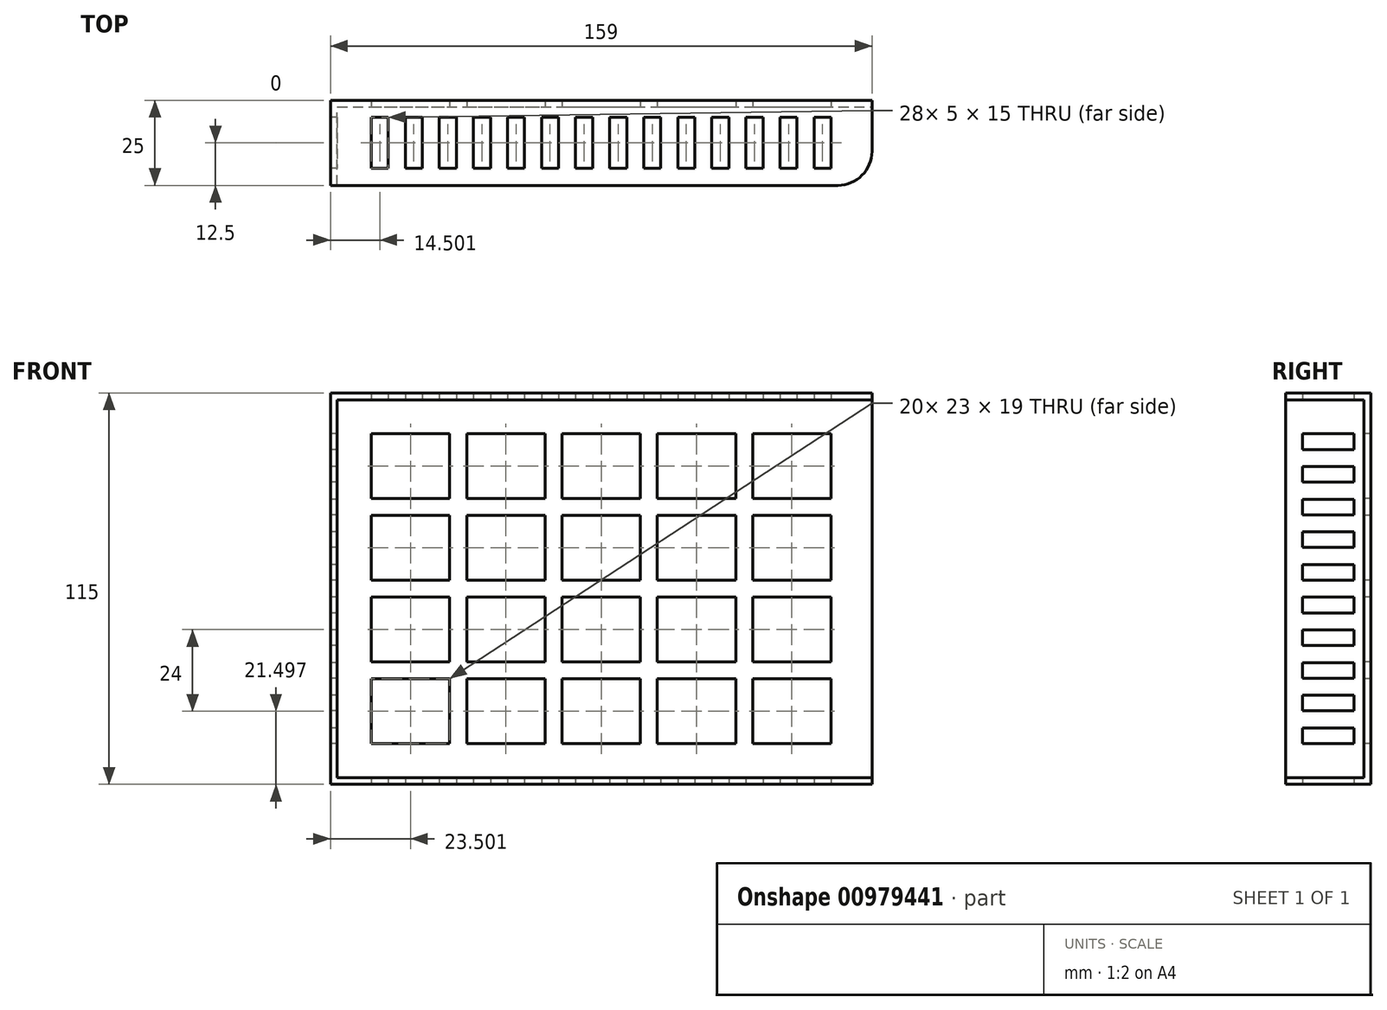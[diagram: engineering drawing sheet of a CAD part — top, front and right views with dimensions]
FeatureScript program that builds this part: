
annotation { "Feature Type Name" : "Feature", "Feature Type Description" : "" }
export const myFeature = defineFeature(function(context is Context, id is Id, definition is map)
    precondition{}
    {
        {
            var Q0;
            Q0=qCreatedBy(makeId("Front.planeOp"),FACE);
            var sketch = newSketch(context, id + "F0", { "sketchPlane" : qUnion([Q0])});
            skLineSegment(sketch, "E0.bottom", {"start": v(-112.02, 69.3) * mm, "end": v(46.98, 69.3) * mm});
            skLineSegment(sketch, "E0.top", {"start": v(-112.02, -45.7) * mm, "end": v(46.98, -45.7) * mm});
            skLineSegment(sketch, "E0.left", {"start": v(-112.02, 69.3) * mm, "end": v(-112.02, -45.7) * mm});
            skLineSegment(sketch, "E0.right", {"start": v(46.98, 69.3) * mm, "end": v(46.98, -45.7) * mm});
            skSolve(sketch);
        }
        {
            var Q0;
            Q0=makeQuery(id+"F0.imprint","IMPRINT",FACE,{"disambiguationData":[TD([[makeQuery(id+"F0.imprint","IMPRINT",EDGE,{"derivedFrom":sQuery(id+"F0.wireOp",EDGE,"E0.bottom")}),-1.0]])]});
            extrude(context, id + "F1", {"entities" : qUnion([Q0]), "depth" : 25 * mm, "offsetDistance" : 25 * mm});
        }
        {
            var Q0;
            Q0=makeQuery(id+"F1.opExtrude","CAP_FACE",FACE,{"disambiguationData":[OSD([sQuery(id+"F0.wireOp",EDGE,"E0.bottom"),sQuery(id+"F0.wireOp",EDGE,"E0.top"),sQuery(id+"F0.wireOp",EDGE,"E0.left"),sQuery(id+"F0.wireOp",EDGE,"E0.right")])],"isStart":false});
            var Q1;
            Q1=makeQuery(id+"F1.opExtrude","SWEPT_FACE",FACE,{"disambiguationData":[OSD([sQuery(id+"F0.wireOp",EDGE,"E0.right")])]});
            shell(context, id + "F2", {"entities" : qUnion([Q0, Q1]), "thickness" : 2 * mm});
        }
        {
            var Q0;
            Q0=makeQuery(id+"F1.opExtrude","CAP_EDGE",EDGE,{"disambiguationData":[OSD([sQuery(id+"F0.wireOp",EDGE,"E0.right")])],"isStart":false});
            var Q1;
            {var subQ0=sQuery(id+"F0.wireOp",EDGE,"E0.right");Q1=makeQuery(id+"F2.opShell","OFFSET_EDGE",EDGE,{"disambiguationData":[OSD([subQ0]),TDD([makeQuery(id+"F1.opExtrude","CAP_EDGE",EDGE,{"disambiguationData":[OSD([subQ0])],"isStart":false})])]});}
            fillet(context, id + "F3", {"entities" : qUnion([Q0, Q1]), "radius" : 10 * mm, "tangentPropagation" : true, "allowEdgeOverflow" : false});
        }
        {
            var Q0;
            Q0=makeQuery(id+"F2.opShell","OFFSET_FACE",FACE,{"disambiguationData":[OSD([sQuery(id+"F0.wireOp",EDGE,"E0.bottom"),sQuery(id+"F0.wireOp",EDGE,"E0.top"),sQuery(id+"F0.wireOp",EDGE,"E0.left"),sQuery(id+"F0.wireOp",EDGE,"E0.right")])]});
            var sketch = newSketch(context, id + "F4", { "sketchPlane" : qUnion([Q0])});
            skLineSegment(sketch, "E1.bottom", {"start": v(-100.02, 57.3) * mm, "end": v(-77.02, 57.3) * mm});
            skLineSegment(sketch, "E1.top", {"start": v(-100.02, 38.3) * mm, "end": v(-77.02, 38.3) * mm});
            skLineSegment(sketch, "E1.left", {"start": v(-100.02, 57.3) * mm, "end": v(-100.02, 38.3) * mm});
            skLineSegment(sketch, "E1.right", {"start": v(-77.02, 57.3) * mm, "end": v(-77.02, 38.3) * mm});
            skLineSegment(sketch, "E2.0.1.0", {"start": v(-100.02, 33.3) * mm, "end": v(-77.02, 33.3) * mm});
            skLineSegment(sketch, "E2.0.1.1", {"start": v(-77.02, 33.3) * mm, "end": v(-77.02, 14.3) * mm});
            skLineSegment(sketch, "E2.0.1.2", {"start": v(-100.02, 14.3) * mm, "end": v(-77.02, 14.3) * mm});
            skLineSegment(sketch, "E2.0.1.3", {"start": v(-100.02, 33.3) * mm, "end": v(-100.02, 14.3) * mm});
            skLineSegment(sketch, "E2.0.2.0", {"start": v(-100.02, 9.3) * mm, "end": v(-77.02, 9.3) * mm});
            skLineSegment(sketch, "E2.0.2.1", {"start": v(-77.02, 9.3) * mm, "end": v(-77.02, -9.7) * mm});
            skLineSegment(sketch, "E2.0.2.2", {"start": v(-100.02, -9.7) * mm, "end": v(-77.02, -9.7) * mm});
            skLineSegment(sketch, "E2.0.2.3", {"start": v(-100.02, 9.3) * mm, "end": v(-100.02, -9.7) * mm});
            skLineSegment(sketch, "E2.0.3.0", {"start": v(-100.02, -14.7) * mm, "end": v(-77.02, -14.7) * mm});
            skLineSegment(sketch, "E2.0.3.1", {"start": v(-77.02, -14.7) * mm, "end": v(-77.02, -33.7) * mm});
            skLineSegment(sketch, "E2.0.3.2", {"start": v(-100.02, -33.7) * mm, "end": v(-77.02, -33.7) * mm});
            skLineSegment(sketch, "E2.0.3.3", {"start": v(-100.02, -14.7) * mm, "end": v(-100.02, -33.7) * mm});
            skLineSegment(sketch, "E2.1.0.0", {"start": v(-72.02, 57.3) * mm, "end": v(-49.02, 57.3) * mm});
            skLineSegment(sketch, "E2.1.0.1", {"start": v(-49.02, 57.3) * mm, "end": v(-49.02, 38.3) * mm});
            skLineSegment(sketch, "E2.1.0.2", {"start": v(-72.02, 38.3) * mm, "end": v(-49.02, 38.3) * mm});
            skLineSegment(sketch, "E2.1.0.3", {"start": v(-72.02, 57.3) * mm, "end": v(-72.02, 38.3) * mm});
            skLineSegment(sketch, "E2.1.1.0", {"start": v(-72.02, 33.3) * mm, "end": v(-49.02, 33.3) * mm});
            skLineSegment(sketch, "E2.1.1.1", {"start": v(-49.02, 33.3) * mm, "end": v(-49.02, 14.3) * mm});
            skLineSegment(sketch, "E2.1.1.2", {"start": v(-72.02, 14.3) * mm, "end": v(-49.02, 14.3) * mm});
            skLineSegment(sketch, "E2.1.1.3", {"start": v(-72.02, 33.3) * mm, "end": v(-72.02, 14.3) * mm});
            skLineSegment(sketch, "E2.1.2.0", {"start": v(-72.02, 9.3) * mm, "end": v(-49.02, 9.3) * mm});
            skLineSegment(sketch, "E2.1.2.1", {"start": v(-49.02, 9.3) * mm, "end": v(-49.02, -9.7) * mm});
            skLineSegment(sketch, "E2.1.2.2", {"start": v(-72.02, -9.7) * mm, "end": v(-49.02, -9.7) * mm});
            skLineSegment(sketch, "E2.1.2.3", {"start": v(-72.02, 9.3) * mm, "end": v(-72.02, -9.7) * mm});
            skLineSegment(sketch, "E2.1.3.0", {"start": v(-72.02, -14.7) * mm, "end": v(-49.02, -14.7) * mm});
            skLineSegment(sketch, "E2.1.3.1", {"start": v(-49.02, -14.7) * mm, "end": v(-49.02, -33.7) * mm});
            skLineSegment(sketch, "E2.1.3.2", {"start": v(-72.02, -33.7) * mm, "end": v(-49.02, -33.7) * mm});
            skLineSegment(sketch, "E2.1.3.3", {"start": v(-72.02, -14.7) * mm, "end": v(-72.02, -33.7) * mm});
            skLineSegment(sketch, "E2.2.0.0", {"start": v(-44.02, 57.3) * mm, "end": v(-21.02, 57.3) * mm});
            skLineSegment(sketch, "E2.2.0.1", {"start": v(-21.02, 57.3) * mm, "end": v(-21.02, 38.3) * mm});
            skLineSegment(sketch, "E2.2.0.2", {"start": v(-44.02, 38.3) * mm, "end": v(-21.02, 38.3) * mm});
            skLineSegment(sketch, "E2.2.0.3", {"start": v(-44.02, 57.3) * mm, "end": v(-44.02, 38.3) * mm});
            skLineSegment(sketch, "E2.2.1.0", {"start": v(-44.02, 33.3) * mm, "end": v(-21.02, 33.3) * mm});
            skLineSegment(sketch, "E2.2.1.1", {"start": v(-21.02, 33.3) * mm, "end": v(-21.02, 14.3) * mm});
            skLineSegment(sketch, "E2.2.1.2", {"start": v(-44.02, 14.3) * mm, "end": v(-21.02, 14.3) * mm});
            skLineSegment(sketch, "E2.2.1.3", {"start": v(-44.02, 33.3) * mm, "end": v(-44.02, 14.3) * mm});
            skLineSegment(sketch, "E2.2.2.0", {"start": v(-44.02, 9.3) * mm, "end": v(-21.02, 9.3) * mm});
            skLineSegment(sketch, "E2.2.2.1", {"start": v(-21.02, 9.3) * mm, "end": v(-21.02, -9.7) * mm});
            skLineSegment(sketch, "E2.2.2.2", {"start": v(-44.02, -9.7) * mm, "end": v(-21.02, -9.7) * mm});
            skLineSegment(sketch, "E2.2.2.3", {"start": v(-44.02, 9.3) * mm, "end": v(-44.02, -9.7) * mm});
            skLineSegment(sketch, "E2.2.3.0", {"start": v(-44.02, -14.7) * mm, "end": v(-21.02, -14.7) * mm});
            skLineSegment(sketch, "E2.2.3.1", {"start": v(-21.02, -14.7) * mm, "end": v(-21.02, -33.7) * mm});
            skLineSegment(sketch, "E2.2.3.2", {"start": v(-44.02, -33.7) * mm, "end": v(-21.02, -33.7) * mm});
            skLineSegment(sketch, "E2.2.3.3", {"start": v(-44.02, -14.7) * mm, "end": v(-44.02, -33.7) * mm});
            skLineSegment(sketch, "E2.3.0.0", {"start": v(-16.02, 57.3) * mm, "end": v(6.98, 57.3) * mm});
            skLineSegment(sketch, "E2.3.0.1", {"start": v(6.98, 57.3) * mm, "end": v(6.98, 38.3) * mm});
            skLineSegment(sketch, "E2.3.0.2", {"start": v(-16.02, 38.3) * mm, "end": v(6.98, 38.3) * mm});
            skLineSegment(sketch, "E2.3.0.3", {"start": v(-16.02, 57.3) * mm, "end": v(-16.02, 38.3) * mm});
            skLineSegment(sketch, "E2.3.1.0", {"start": v(-16.02, 33.3) * mm, "end": v(6.98, 33.3) * mm});
            skLineSegment(sketch, "E2.3.1.1", {"start": v(6.98, 33.3) * mm, "end": v(6.98, 14.3) * mm});
            skLineSegment(sketch, "E2.3.1.2", {"start": v(-16.02, 14.3) * mm, "end": v(6.98, 14.3) * mm});
            skLineSegment(sketch, "E2.3.1.3", {"start": v(-16.02, 33.3) * mm, "end": v(-16.02, 14.3) * mm});
            skLineSegment(sketch, "E2.3.2.0", {"start": v(-16.02, 9.3) * mm, "end": v(6.98, 9.3) * mm});
            skLineSegment(sketch, "E2.3.2.1", {"start": v(6.98, 9.3) * mm, "end": v(6.98, -9.7) * mm});
            skLineSegment(sketch, "E2.3.2.2", {"start": v(-16.02, -9.7) * mm, "end": v(6.98, -9.7) * mm});
            skLineSegment(sketch, "E2.3.2.3", {"start": v(-16.02, 9.3) * mm, "end": v(-16.02, -9.7) * mm});
            skLineSegment(sketch, "E2.3.3.0", {"start": v(-16.02, -14.7) * mm, "end": v(6.98, -14.7) * mm});
            skLineSegment(sketch, "E2.3.3.1", {"start": v(6.98, -14.7) * mm, "end": v(6.98, -33.7) * mm});
            skLineSegment(sketch, "E2.3.3.2", {"start": v(-16.02, -33.7) * mm, "end": v(6.98, -33.7) * mm});
            skLineSegment(sketch, "E2.3.3.3", {"start": v(-16.02, -14.7) * mm, "end": v(-16.02, -33.7) * mm});
            skLineSegment(sketch, "E2.4.0.0", {"start": v(11.98, 57.3) * mm, "end": v(34.98, 57.3) * mm});
            skLineSegment(sketch, "E2.4.0.1", {"start": v(34.98, 57.3) * mm, "end": v(34.98, 38.3) * mm});
            skLineSegment(sketch, "E2.4.0.2", {"start": v(11.98, 38.3) * mm, "end": v(34.98, 38.3) * mm});
            skLineSegment(sketch, "E2.4.0.3", {"start": v(11.98, 57.3) * mm, "end": v(11.98, 38.3) * mm});
            skLineSegment(sketch, "E2.4.1.0", {"start": v(11.98, 33.3) * mm, "end": v(34.98, 33.3) * mm});
            skLineSegment(sketch, "E2.4.1.1", {"start": v(34.98, 33.3) * mm, "end": v(34.98, 14.3) * mm});
            skLineSegment(sketch, "E2.4.1.2", {"start": v(11.98, 14.3) * mm, "end": v(34.98, 14.3) * mm});
            skLineSegment(sketch, "E2.4.1.3", {"start": v(11.98, 33.3) * mm, "end": v(11.98, 14.3) * mm});
            skLineSegment(sketch, "E2.4.2.0", {"start": v(11.98, 9.3) * mm, "end": v(34.98, 9.3) * mm});
            skLineSegment(sketch, "E2.4.2.1", {"start": v(34.98, 9.3) * mm, "end": v(34.98, -9.7) * mm});
            skLineSegment(sketch, "E2.4.2.2", {"start": v(11.98, -9.7) * mm, "end": v(34.98, -9.7) * mm});
            skLineSegment(sketch, "E2.4.2.3", {"start": v(11.98, 9.3) * mm, "end": v(11.98, -9.7) * mm});
            skLineSegment(sketch, "E2.4.3.0", {"start": v(11.98, -14.7) * mm, "end": v(34.98, -14.7) * mm});
            skLineSegment(sketch, "E2.4.3.1", {"start": v(34.98, -14.7) * mm, "end": v(34.98, -33.7) * mm});
            skLineSegment(sketch, "E2.4.3.2", {"start": v(11.98, -33.7) * mm, "end": v(34.98, -33.7) * mm});
            skLineSegment(sketch, "E2.4.3.3", {"start": v(11.98, -14.7) * mm, "end": v(11.98, -33.7) * mm});
            skLineSegment(sketch, "E2.direction1", {"start": v(-100.02, 57.3) * mm, "end": v(-72.02, 57.3) * mm, "construction": true});
            skLineSegment(sketch, "E2.direction2", {"start": v(-100.02, 57.3) * mm, "end": v(-100.02, 33.3) * mm, "construction": true});
            skPoint(sketch, "E3.top.end.orphan", {"position": v(-100.02, -33.7) * mm});
            skSolve(sketch);
        }
        {
            var Q0;
            Q0=makeQuery(id+"F4.imprint","IMPRINT",FACE,{"disambiguationData":[TD([[makeQuery(id+"F4.imprint","IMPRINT",EDGE,{"derivedFrom":sQuery(id+"F4.wireOp",EDGE,"E1.bottom")}),-1.0]])]});
            var Q1;
            Q1=makeQuery(id+"F4.imprint","IMPRINT",FACE,{"disambiguationData":[TD([[makeQuery(id+"F4.imprint","IMPRINT",EDGE,{"derivedFrom":sQuery(id+"F4.wireOp",EDGE,"E2.1.0.0")}),-1.0]])]});
            var Q2;
            Q2=makeQuery(id+"F4.imprint","IMPRINT",FACE,{"disambiguationData":[TD([[makeQuery(id+"F4.imprint","IMPRINT",EDGE,{"derivedFrom":sQuery(id+"F4.wireOp",EDGE,"E2.2.0.0")}),-1.0]])]});
            var Q3;
            Q3=makeQuery(id+"F4.imprint","IMPRINT",FACE,{"disambiguationData":[TD([[makeQuery(id+"F4.imprint","IMPRINT",EDGE,{"derivedFrom":sQuery(id+"F4.wireOp",EDGE,"E2.3.0.0")}),-1.0]])]});
            var Q4;
            Q4=makeQuery(id+"F4.imprint","IMPRINT",FACE,{"disambiguationData":[TD([[makeQuery(id+"F4.imprint","IMPRINT",EDGE,{"derivedFrom":sQuery(id+"F4.wireOp",EDGE,"E2.4.0.0")}),-1.0]])]});
            var Q5;
            Q5=makeQuery(id+"F4.imprint","IMPRINT",FACE,{"disambiguationData":[TD([[makeQuery(id+"F4.imprint","IMPRINT",EDGE,{"derivedFrom":sQuery(id+"F4.wireOp",EDGE,"E2.0.1.0")}),-1.0]])]});
            var Q6;
            Q6=makeQuery(id+"F4.imprint","IMPRINT",FACE,{"disambiguationData":[TD([[makeQuery(id+"F4.imprint","IMPRINT",EDGE,{"derivedFrom":sQuery(id+"F4.wireOp",EDGE,"E2.1.1.0")}),-1.0]])]});
            var Q7;
            Q7=makeQuery(id+"F4.imprint","IMPRINT",FACE,{"disambiguationData":[TD([[makeQuery(id+"F4.imprint","IMPRINT",EDGE,{"derivedFrom":sQuery(id+"F4.wireOp",EDGE,"E2.2.1.0")}),-1.0]])]});
            var Q8;
            Q8=makeQuery(id+"F4.imprint","IMPRINT",FACE,{"disambiguationData":[TD([[makeQuery(id+"F4.imprint","IMPRINT",EDGE,{"derivedFrom":sQuery(id+"F4.wireOp",EDGE,"E2.3.1.0")}),-1.0]])]});
            var Q9;
            Q9=makeQuery(id+"F4.imprint","IMPRINT",FACE,{"disambiguationData":[TD([[makeQuery(id+"F4.imprint","IMPRINT",EDGE,{"derivedFrom":sQuery(id+"F4.wireOp",EDGE,"E2.4.1.0")}),-1.0]])]});
            var Q10;
            Q10=makeQuery(id+"F4.imprint","IMPRINT",FACE,{"disambiguationData":[TD([[makeQuery(id+"F4.imprint","IMPRINT",EDGE,{"derivedFrom":sQuery(id+"F4.wireOp",EDGE,"E2.4.2.0")}),-1.0]])]});
            var Q11;
            Q11=makeQuery(id+"F4.imprint","IMPRINT",FACE,{"disambiguationData":[TD([[makeQuery(id+"F4.imprint","IMPRINT",EDGE,{"derivedFrom":sQuery(id+"F4.wireOp",EDGE,"E2.3.2.0")}),-1.0]])]});
            var Q12;
            Q12=makeQuery(id+"F4.imprint","IMPRINT",FACE,{"disambiguationData":[TD([[makeQuery(id+"F4.imprint","IMPRINT",EDGE,{"derivedFrom":sQuery(id+"F4.wireOp",EDGE,"E2.2.2.0")}),-1.0]])]});
            var Q13;
            Q13=makeQuery(id+"F4.imprint","IMPRINT",FACE,{"disambiguationData":[TD([[makeQuery(id+"F4.imprint","IMPRINT",EDGE,{"derivedFrom":sQuery(id+"F4.wireOp",EDGE,"E2.1.2.0")}),-1.0]])]});
            var Q14;
            Q14=makeQuery(id+"F4.imprint","IMPRINT",FACE,{"disambiguationData":[TD([[makeQuery(id+"F4.imprint","IMPRINT",EDGE,{"derivedFrom":sQuery(id+"F4.wireOp",EDGE,"E2.0.2.0")}),-1.0]])]});
            var Q15;
            Q15=makeQuery(id+"F4.imprint","IMPRINT",FACE,{"disambiguationData":[TD([[makeQuery(id+"F4.imprint","IMPRINT",EDGE,{"derivedFrom":sQuery(id+"F4.wireOp",EDGE,"E2.0.3.0")}),-1.0]])]});
            var Q16;
            Q16=makeQuery(id+"F4.imprint","IMPRINT",FACE,{"disambiguationData":[TD([[makeQuery(id+"F4.imprint","IMPRINT",EDGE,{"derivedFrom":sQuery(id+"F4.wireOp",EDGE,"E2.1.3.0")}),-1.0]])]});
            var Q17;
            Q17=makeQuery(id+"F4.imprint","IMPRINT",FACE,{"disambiguationData":[TD([[makeQuery(id+"F4.imprint","IMPRINT",EDGE,{"derivedFrom":sQuery(id+"F4.wireOp",EDGE,"E2.2.3.0")}),-1.0]])]});
            var Q18;
            Q18=makeQuery(id+"F4.imprint","IMPRINT",FACE,{"disambiguationData":[TD([[makeQuery(id+"F4.imprint","IMPRINT",EDGE,{"derivedFrom":sQuery(id+"F4.wireOp",EDGE,"E2.3.3.0")}),-1.0]])]});
            var Q19;
            Q19=makeQuery(id+"F4.imprint","IMPRINT",FACE,{"disambiguationData":[TD([[makeQuery(id+"F4.imprint","IMPRINT",EDGE,{"derivedFrom":sQuery(id+"F4.wireOp",EDGE,"E2.4.3.0")}),-1.0]])]});
            extrude(context, id + "F5", {"entities" : qUnion([Q0, Q1, Q2, Q3, Q4, Q5, Q6, Q7, Q8, Q9, Q10, Q11, Q12, Q13, Q14, Q15, Q16, Q17, Q18, Q19]), "operationType" : NewBodyOperationType.REMOVE, "oppositeDirection" : true, "depth" : 25 * mm, "offsetDistance" : 25 * mm});
        }
        {
            var Q0;
            Q0=makeQuery(id+"F1.opExtrude","SWEPT_FACE",FACE,{"disambiguationData":[OSD([sQuery(id+"F0.wireOp",EDGE,"E0.top")])]});
            var sketch = newSketch(context, id + "F6", { "sketchPlane" : qUnion([Q0])});
            skLineSegment(sketch, "E4.bottom", {"start": v(-100.02, 20) * mm, "end": v(-95.02, 20) * mm});
            skLineSegment(sketch, "E4.top", {"start": v(-100.02, 5) * mm, "end": v(-95.02, 5) * mm});
            skLineSegment(sketch, "E4.left", {"start": v(-100.02, 20) * mm, "end": v(-100.02, 5) * mm});
            skLineSegment(sketch, "E4.right", {"start": v(-95.02, 20) * mm, "end": v(-95.02, 5) * mm});
            skLineSegment(sketch, "E5.1.0.0", {"start": v(-85.02, 20) * mm, "end": v(-85.02, 5) * mm});
            skLineSegment(sketch, "E5.1.0.1", {"start": v(-90.02, 20) * mm, "end": v(-85.02, 20) * mm});
            skLineSegment(sketch, "E5.1.0.2", {"start": v(-90.02, 20) * mm, "end": v(-90.02, 5) * mm});
            skLineSegment(sketch, "E5.1.0.3", {"start": v(-90.02, 5) * mm, "end": v(-85.02, 5) * mm});
            skLineSegment(sketch, "E5.2.0.0", {"start": v(-75.02, 20) * mm, "end": v(-75.02, 5) * mm});
            skLineSegment(sketch, "E5.2.0.1", {"start": v(-80.02, 20) * mm, "end": v(-75.02, 20) * mm});
            skLineSegment(sketch, "E5.2.0.2", {"start": v(-80.02, 20) * mm, "end": v(-80.02, 5) * mm});
            skLineSegment(sketch, "E5.2.0.3", {"start": v(-80.02, 5) * mm, "end": v(-75.02, 5) * mm});
            skLineSegment(sketch, "E5.3.0.0", {"start": v(-65.02, 20) * mm, "end": v(-65.02, 5) * mm});
            skLineSegment(sketch, "E5.3.0.1", {"start": v(-70.02, 20) * mm, "end": v(-65.02, 20) * mm});
            skLineSegment(sketch, "E5.3.0.2", {"start": v(-70.02, 20) * mm, "end": v(-70.02, 5) * mm});
            skLineSegment(sketch, "E5.3.0.3", {"start": v(-70.02, 5) * mm, "end": v(-65.02, 5) * mm});
            skLineSegment(sketch, "E5.4.0.0", {"start": v(-55.02, 20) * mm, "end": v(-55.02, 5) * mm});
            skLineSegment(sketch, "E5.4.0.1", {"start": v(-60.02, 20) * mm, "end": v(-55.02, 20) * mm});
            skLineSegment(sketch, "E5.4.0.2", {"start": v(-60.02, 20) * mm, "end": v(-60.02, 5) * mm});
            skLineSegment(sketch, "E5.4.0.3", {"start": v(-60.02, 5) * mm, "end": v(-55.02, 5) * mm});
            skLineSegment(sketch, "E5.5.0.0", {"start": v(-45.02, 20) * mm, "end": v(-45.02, 5) * mm});
            skLineSegment(sketch, "E5.5.0.1", {"start": v(-50.02, 20) * mm, "end": v(-45.02, 20) * mm});
            skLineSegment(sketch, "E5.5.0.2", {"start": v(-50.02, 20) * mm, "end": v(-50.02, 5) * mm});
            skLineSegment(sketch, "E5.5.0.3", {"start": v(-50.02, 5) * mm, "end": v(-45.02, 5) * mm});
            skLineSegment(sketch, "E5.6.0.0", {"start": v(-35.02, 20) * mm, "end": v(-35.02, 5) * mm});
            skLineSegment(sketch, "E5.6.0.1", {"start": v(-40.02, 20) * mm, "end": v(-35.02, 20) * mm});
            skLineSegment(sketch, "E5.6.0.2", {"start": v(-40.02, 20) * mm, "end": v(-40.02, 5) * mm});
            skLineSegment(sketch, "E5.6.0.3", {"start": v(-40.02, 5) * mm, "end": v(-35.02, 5) * mm});
            skLineSegment(sketch, "E5.7.0.0", {"start": v(-25.02, 20) * mm, "end": v(-25.02, 5) * mm});
            skLineSegment(sketch, "E5.7.0.1", {"start": v(-30.02, 20) * mm, "end": v(-25.02, 20) * mm});
            skLineSegment(sketch, "E5.7.0.2", {"start": v(-30.02, 20) * mm, "end": v(-30.02, 5) * mm});
            skLineSegment(sketch, "E5.7.0.3", {"start": v(-30.02, 5) * mm, "end": v(-25.02, 5) * mm});
            skLineSegment(sketch, "E5.8.0.0", {"start": v(-15.02, 20) * mm, "end": v(-15.02, 5) * mm});
            skLineSegment(sketch, "E5.8.0.1", {"start": v(-20.02, 20) * mm, "end": v(-15.02, 20) * mm});
            skLineSegment(sketch, "E5.8.0.2", {"start": v(-20.02, 20) * mm, "end": v(-20.02, 5) * mm});
            skLineSegment(sketch, "E5.8.0.3", {"start": v(-20.02, 5) * mm, "end": v(-15.02, 5) * mm});
            skLineSegment(sketch, "E5.9.0.0", {"start": v(-5.02, 20) * mm, "end": v(-5.02, 5) * mm});
            skLineSegment(sketch, "E5.9.0.1", {"start": v(-10.02, 20) * mm, "end": v(-5.02, 20) * mm});
            skLineSegment(sketch, "E5.9.0.2", {"start": v(-10.02, 20) * mm, "end": v(-10.02, 5) * mm});
            skLineSegment(sketch, "E5.9.0.3", {"start": v(-10.02, 5) * mm, "end": v(-5.02, 5) * mm});
            skLineSegment(sketch, "E5.10.0.0", {"start": v(4.98, 20) * mm, "end": v(4.98, 5) * mm});
            skLineSegment(sketch, "E5.10.0.1", {"start": v(-0.02, 20) * mm, "end": v(4.98, 20) * mm});
            skLineSegment(sketch, "E5.10.0.2", {"start": v(-0.02, 20) * mm, "end": v(-0.02, 5) * mm});
            skLineSegment(sketch, "E5.10.0.3", {"start": v(-0.02, 5) * mm, "end": v(4.98, 5) * mm});
            skLineSegment(sketch, "E5.11.0.0", {"start": v(14.98, 20) * mm, "end": v(14.98, 5) * mm});
            skLineSegment(sketch, "E5.11.0.1", {"start": v(9.98, 20) * mm, "end": v(14.98, 20) * mm});
            skLineSegment(sketch, "E5.11.0.2", {"start": v(9.98, 20) * mm, "end": v(9.98, 5) * mm});
            skLineSegment(sketch, "E5.11.0.3", {"start": v(9.98, 5) * mm, "end": v(14.98, 5) * mm});
            skLineSegment(sketch, "E5.12.0.0", {"start": v(24.98, 20) * mm, "end": v(24.98, 5) * mm});
            skLineSegment(sketch, "E5.12.0.1", {"start": v(19.98, 20) * mm, "end": v(24.98, 20) * mm});
            skLineSegment(sketch, "E5.12.0.2", {"start": v(19.98, 20) * mm, "end": v(19.98, 5) * mm});
            skLineSegment(sketch, "E5.12.0.3", {"start": v(19.98, 5) * mm, "end": v(24.98, 5) * mm});
            skLineSegment(sketch, "E5.13.0.0", {"start": v(34.98, 20) * mm, "end": v(34.98, 5) * mm});
            skLineSegment(sketch, "E5.13.0.1", {"start": v(29.98, 20) * mm, "end": v(34.98, 20) * mm});
            skLineSegment(sketch, "E5.13.0.2", {"start": v(29.98, 20) * mm, "end": v(29.98, 5) * mm});
            skLineSegment(sketch, "E5.13.0.3", {"start": v(29.98, 5) * mm, "end": v(34.98, 5) * mm});
            skLineSegment(sketch, "E5.direction1", {"start": v(-95.02, 5) * mm, "end": v(-85.02, 5) * mm, "construction": true});
            skPoint(sketch, "E6.right.end.orphan", {"position": v(-100.02, 5) * mm});
            skSolve(sketch);
        }
        {
            var Q0;
            Q0=makeQuery(id+"F6.imprint","IMPRINT",FACE,{"disambiguationData":[TD([[makeQuery(id+"F6.imprint","IMPRINT",EDGE,{"derivedFrom":sQuery(id+"F6.wireOp",EDGE,"E4.bottom")}),-1.0]])]});
            var Q1;
            Q1=makeQuery(id+"F6.imprint","IMPRINT",FACE,{"disambiguationData":[TD([[makeQuery(id+"F6.imprint","IMPRINT",EDGE,{"derivedFrom":sQuery(id+"F6.wireOp",EDGE,"E5.1.0.0")}),-1.0]])]});
            var Q2;
            Q2=makeQuery(id+"F6.imprint","IMPRINT",FACE,{"disambiguationData":[TD([[makeQuery(id+"F6.imprint","IMPRINT",EDGE,{"derivedFrom":sQuery(id+"F6.wireOp",EDGE,"E5.2.0.0")}),-1.0]])]});
            var Q3;
            Q3=makeQuery(id+"F6.imprint","IMPRINT",FACE,{"disambiguationData":[TD([[makeQuery(id+"F6.imprint","IMPRINT",EDGE,{"derivedFrom":sQuery(id+"F6.wireOp",EDGE,"E5.3.0.0")}),-1.0]])]});
            var Q4;
            Q4=makeQuery(id+"F6.imprint","IMPRINT",FACE,{"disambiguationData":[TD([[makeQuery(id+"F6.imprint","IMPRINT",EDGE,{"derivedFrom":sQuery(id+"F6.wireOp",EDGE,"E5.4.0.0")}),-1.0]])]});
            var Q5;
            Q5=makeQuery(id+"F6.imprint","IMPRINT",FACE,{"disambiguationData":[TD([[makeQuery(id+"F6.imprint","IMPRINT",EDGE,{"derivedFrom":sQuery(id+"F6.wireOp",EDGE,"E5.5.0.0")}),-1.0]])]});
            var Q6;
            Q6=makeQuery(id+"F6.imprint","IMPRINT",FACE,{"disambiguationData":[TD([[makeQuery(id+"F6.imprint","IMPRINT",EDGE,{"derivedFrom":sQuery(id+"F6.wireOp",EDGE,"E5.6.0.0")}),-1.0]])]});
            var Q7;
            Q7=makeQuery(id+"F6.imprint","IMPRINT",FACE,{"disambiguationData":[TD([[makeQuery(id+"F6.imprint","IMPRINT",EDGE,{"derivedFrom":sQuery(id+"F6.wireOp",EDGE,"E5.7.0.0")}),-1.0]])]});
            var Q8;
            Q8=makeQuery(id+"F6.imprint","IMPRINT",FACE,{"disambiguationData":[TD([[makeQuery(id+"F6.imprint","IMPRINT",EDGE,{"derivedFrom":sQuery(id+"F6.wireOp",EDGE,"E5.8.0.0")}),-1.0]])]});
            var Q9;
            Q9=makeQuery(id+"F6.imprint","IMPRINT",FACE,{"disambiguationData":[TD([[makeQuery(id+"F6.imprint","IMPRINT",EDGE,{"derivedFrom":sQuery(id+"F6.wireOp",EDGE,"E5.9.0.0")}),-1.0]])]});
            var Q10;
            Q10=makeQuery(id+"F6.imprint","IMPRINT",FACE,{"disambiguationData":[TD([[makeQuery(id+"F6.imprint","IMPRINT",EDGE,{"derivedFrom":sQuery(id+"F6.wireOp",EDGE,"E5.10.0.0")}),-1.0]])]});
            var Q11;
            Q11=makeQuery(id+"F6.imprint","IMPRINT",FACE,{"disambiguationData":[TD([[makeQuery(id+"F6.imprint","IMPRINT",EDGE,{"derivedFrom":sQuery(id+"F6.wireOp",EDGE,"E5.11.0.0")}),-1.0]])]});
            var Q12;
            Q12=makeQuery(id+"F6.imprint","IMPRINT",FACE,{"disambiguationData":[TD([[makeQuery(id+"F6.imprint","IMPRINT",EDGE,{"derivedFrom":sQuery(id+"F6.wireOp",EDGE,"E5.12.0.0")}),-1.0]])]});
            var Q13;
            Q13=makeQuery(id+"F6.imprint","IMPRINT",FACE,{"disambiguationData":[TD([[makeQuery(id+"F6.imprint","IMPRINT",EDGE,{"derivedFrom":sQuery(id+"F6.wireOp",EDGE,"E5.13.0.0")}),-1.0]])]});
            extrude(context, id + "F7", {"entities" : qUnion([Q0, Q1, Q2, Q3, Q4, Q5, Q6, Q7, Q8, Q9, Q10, Q11, Q12, Q13]), "operationType" : NewBodyOperationType.REMOVE, "endBound" : BoundingType.THROUGH_ALL, "oppositeDirection" : true, "depth" : 25 * mm, "offsetDistance" : 25 * mm});
        }
        {
            var Q0;
            Q0=makeQuery(id+"F1.opExtrude","SWEPT_FACE",FACE,{"disambiguationData":[OSD([sQuery(id+"F0.wireOp",EDGE,"E0.left")])]});
            var sketch = newSketch(context, id + "F8", { "sketchPlane" : qUnion([Q0])});
            skLineSegment(sketch, "E7.bottom", {"start": v(20, 57.3) * mm, "end": v(5, 57.3) * mm});
            skLineSegment(sketch, "E7.top", {"start": v(20, 52.7) * mm, "end": v(5, 52.7) * mm});
            skLineSegment(sketch, "E7.left", {"start": v(20, 57.3) * mm, "end": v(20, 52.7) * mm});
            skLineSegment(sketch, "E7.right", {"start": v(5, 57.3) * mm, "end": v(5, 52.7) * mm});
            skLineSegment(sketch, "E8.0.1.0", {"start": v(20, 47.7) * mm, "end": v(20, 43.1) * mm});
            skLineSegment(sketch, "E8.0.1.1", {"start": v(20, 43.1) * mm, "end": v(5, 43.1) * mm});
            skLineSegment(sketch, "E8.0.1.2", {"start": v(20, 47.7) * mm, "end": v(5, 47.7) * mm});
            skLineSegment(sketch, "E8.0.1.3", {"start": v(5, 47.7) * mm, "end": v(5, 43.1) * mm});
            skLineSegment(sketch, "E8.0.2.0", {"start": v(20, 38.1) * mm, "end": v(20, 33.5) * mm});
            skLineSegment(sketch, "E8.0.2.1", {"start": v(20, 33.5) * mm, "end": v(5, 33.5) * mm});
            skLineSegment(sketch, "E8.0.2.2", {"start": v(20, 38.1) * mm, "end": v(5, 38.1) * mm});
            skLineSegment(sketch, "E8.0.2.3", {"start": v(5, 38.1) * mm, "end": v(5, 33.5) * mm});
            skLineSegment(sketch, "E8.0.3.0", {"start": v(20, 28.5) * mm, "end": v(20, 23.9) * mm});
            skLineSegment(sketch, "E8.0.3.1", {"start": v(20, 23.9) * mm, "end": v(5, 23.9) * mm});
            skLineSegment(sketch, "E8.0.3.2", {"start": v(20, 28.5) * mm, "end": v(5, 28.5) * mm});
            skLineSegment(sketch, "E8.0.3.3", {"start": v(5, 28.5) * mm, "end": v(5, 23.9) * mm});
            skLineSegment(sketch, "E8.0.4.0", {"start": v(20, 18.9) * mm, "end": v(20, 14.3) * mm});
            skLineSegment(sketch, "E8.0.4.1", {"start": v(20, 14.3) * mm, "end": v(5, 14.3) * mm});
            skLineSegment(sketch, "E8.0.4.2", {"start": v(20, 18.9) * mm, "end": v(5, 18.9) * mm});
            skLineSegment(sketch, "E8.0.4.3", {"start": v(5, 18.9) * mm, "end": v(5, 14.3) * mm});
            skLineSegment(sketch, "E8.0.5.0", {"start": v(20, 9.3) * mm, "end": v(20, 4.7) * mm});
            skLineSegment(sketch, "E8.0.5.1", {"start": v(20, 4.7) * mm, "end": v(5, 4.7) * mm});
            skLineSegment(sketch, "E8.0.5.2", {"start": v(20, 9.3) * mm, "end": v(5, 9.3) * mm});
            skLineSegment(sketch, "E8.0.5.3", {"start": v(5, 9.3) * mm, "end": v(5, 4.7) * mm});
            skLineSegment(sketch, "E8.0.6.0", {"start": v(20, -0.3) * mm, "end": v(20, -4.9) * mm});
            skLineSegment(sketch, "E8.0.6.1", {"start": v(20, -4.9) * mm, "end": v(5, -4.9) * mm});
            skLineSegment(sketch, "E8.0.6.2", {"start": v(20, -0.3) * mm, "end": v(5, -0.3) * mm});
            skLineSegment(sketch, "E8.0.6.3", {"start": v(5, -0.3) * mm, "end": v(5, -4.9) * mm});
            skLineSegment(sketch, "E8.0.7.0", {"start": v(20, -9.9) * mm, "end": v(20, -14.5) * mm});
            skLineSegment(sketch, "E8.0.7.1", {"start": v(20, -14.5) * mm, "end": v(5, -14.5) * mm});
            skLineSegment(sketch, "E8.0.7.2", {"start": v(20, -9.9) * mm, "end": v(5, -9.9) * mm});
            skLineSegment(sketch, "E8.0.7.3", {"start": v(5, -9.9) * mm, "end": v(5, -14.5) * mm});
            skLineSegment(sketch, "E8.0.8.0", {"start": v(20, -19.5) * mm, "end": v(20, -24.1) * mm});
            skLineSegment(sketch, "E8.0.8.1", {"start": v(20, -24.1) * mm, "end": v(5, -24.1) * mm});
            skLineSegment(sketch, "E8.0.8.2", {"start": v(20, -19.5) * mm, "end": v(5, -19.5) * mm});
            skLineSegment(sketch, "E8.0.8.3", {"start": v(5, -19.5) * mm, "end": v(5, -24.1) * mm});
            skLineSegment(sketch, "E8.0.9.0", {"start": v(20, -29.1) * mm, "end": v(20, -33.7) * mm});
            skLineSegment(sketch, "E8.0.9.1", {"start": v(20, -33.7) * mm, "end": v(5, -33.7) * mm});
            skLineSegment(sketch, "E8.0.9.2", {"start": v(20, -29.1) * mm, "end": v(5, -29.1) * mm});
            skLineSegment(sketch, "E8.0.9.3", {"start": v(5, -29.1) * mm, "end": v(5, -33.7) * mm});
            skLineSegment(sketch, "E8.direction1", {"start": v(20, 52.3) * mm, "end": v(38.8, 52.3) * mm, "construction": true});
            skLineSegment(sketch, "E8.direction2", {"start": v(20, 52.3) * mm, "end": v(20, 42.7) * mm, "construction": true});
            skPoint(sketch, "E9.top.end.orphan", {"position": v(5, 57.3) * mm});
            skPoint(sketch, "E10.top.end.orphan", {"position": v(5, -33.7) * mm});
            skSolve(sketch);
        }
        {
            var Q0;
            Q0=makeQuery(id+"F8.imprint","IMPRINT",FACE,{"disambiguationData":[TD([[makeQuery(id+"F8.imprint","IMPRINT",EDGE,{"derivedFrom":sQuery(id+"F8.wireOp",EDGE,"E7.bottom")}),1.0]])]});
            var Q1;
            Q1=makeQuery(id+"F8.imprint","IMPRINT",FACE,{"disambiguationData":[TD([[makeQuery(id+"F8.imprint","IMPRINT",EDGE,{"derivedFrom":sQuery(id+"F8.wireOp",EDGE,"E8.0.1.0")}),-1.0]])]});
            var Q2;
            Q2=makeQuery(id+"F8.imprint","IMPRINT",FACE,{"disambiguationData":[TD([[makeQuery(id+"F8.imprint","IMPRINT",EDGE,{"derivedFrom":sQuery(id+"F8.wireOp",EDGE,"E8.0.2.0")}),-1.0]])]});
            var Q3;
            Q3=makeQuery(id+"F8.imprint","IMPRINT",FACE,{"disambiguationData":[TD([[makeQuery(id+"F8.imprint","IMPRINT",EDGE,{"derivedFrom":sQuery(id+"F8.wireOp",EDGE,"E8.0.3.0")}),-1.0]])]});
            var Q4;
            Q4=makeQuery(id+"F8.imprint","IMPRINT",FACE,{"disambiguationData":[TD([[makeQuery(id+"F8.imprint","IMPRINT",EDGE,{"derivedFrom":sQuery(id+"F8.wireOp",EDGE,"E8.0.4.0")}),-1.0]])]});
            var Q5;
            Q5=makeQuery(id+"F8.imprint","IMPRINT",FACE,{"disambiguationData":[TD([[makeQuery(id+"F8.imprint","IMPRINT",EDGE,{"derivedFrom":sQuery(id+"F8.wireOp",EDGE,"E8.0.5.0")}),-1.0]])]});
            var Q6;
            Q6=makeQuery(id+"F8.imprint","IMPRINT",FACE,{"disambiguationData":[TD([[makeQuery(id+"F8.imprint","IMPRINT",EDGE,{"derivedFrom":sQuery(id+"F8.wireOp",EDGE,"E8.0.6.0")}),-1.0]])]});
            var Q7;
            Q7=makeQuery(id+"F8.imprint","IMPRINT",FACE,{"disambiguationData":[TD([[makeQuery(id+"F8.imprint","IMPRINT",EDGE,{"derivedFrom":sQuery(id+"F8.wireOp",EDGE,"E8.0.7.0")}),-1.0]])]});
            var Q8;
            Q8=makeQuery(id+"F8.imprint","IMPRINT",FACE,{"disambiguationData":[TD([[makeQuery(id+"F8.imprint","IMPRINT",EDGE,{"derivedFrom":sQuery(id+"F8.wireOp",EDGE,"E8.0.8.0")}),-1.0]])]});
            var Q9;
            Q9=makeQuery(id+"F8.imprint","IMPRINT",FACE,{"disambiguationData":[TD([[makeQuery(id+"F8.imprint","IMPRINT",EDGE,{"derivedFrom":sQuery(id+"F8.wireOp",EDGE,"E8.0.9.0")}),-1.0]])]});
            extrude(context, id + "F9", {"entities" : qUnion([Q0, Q1, Q2, Q3, Q4, Q5, Q6, Q7, Q8, Q9]), "operationType" : NewBodyOperationType.REMOVE, "oppositeDirection" : true, "depth" : 25 * mm, "offsetDistance" : 25 * mm});
        }
    });
